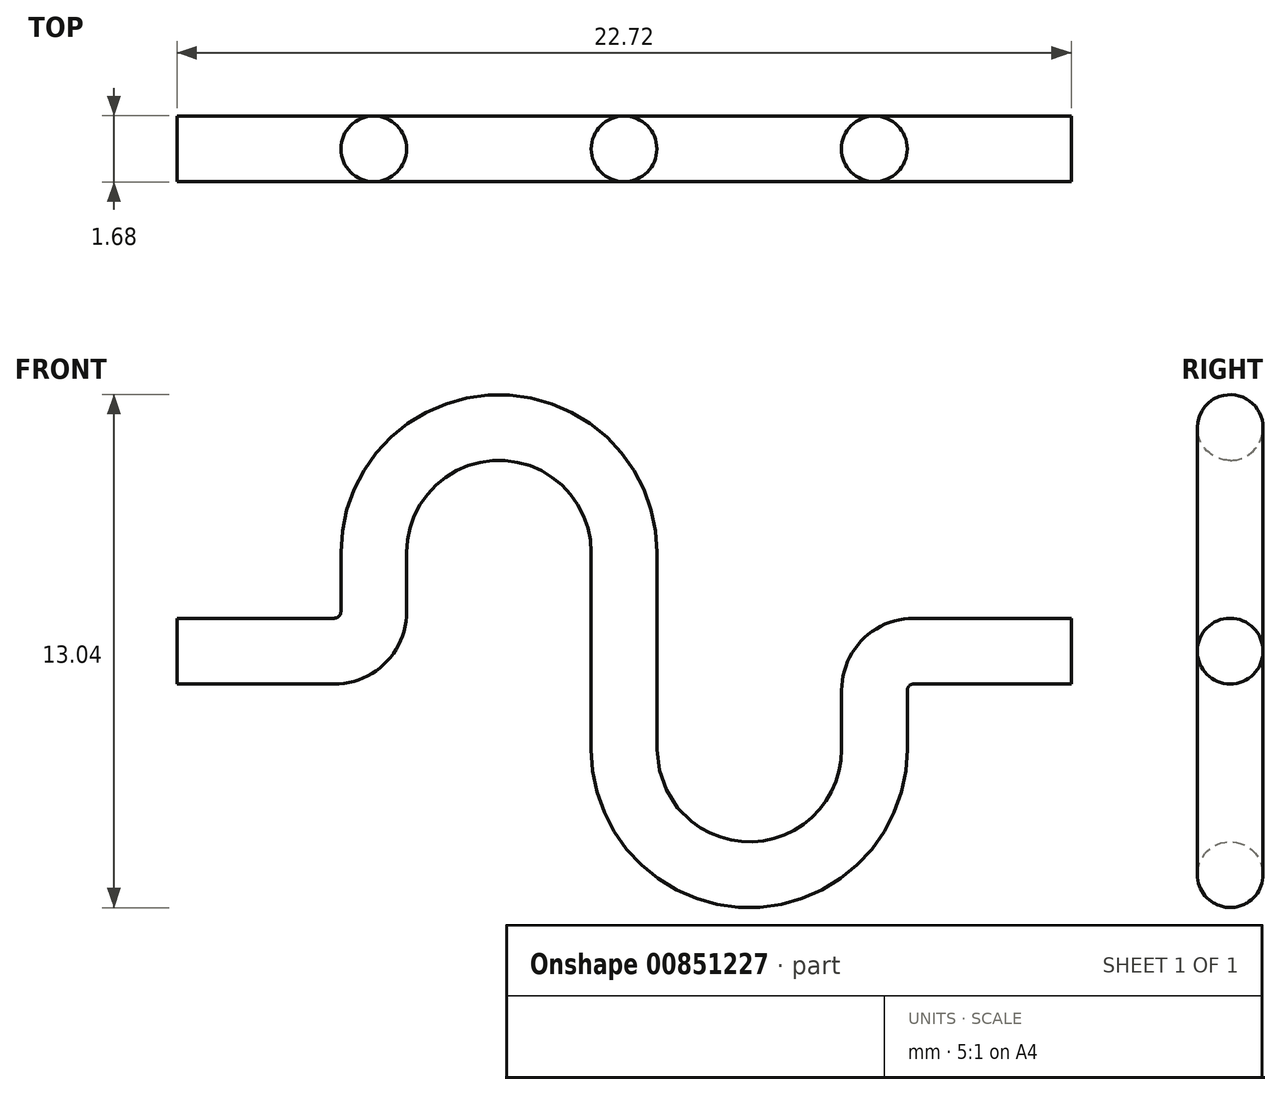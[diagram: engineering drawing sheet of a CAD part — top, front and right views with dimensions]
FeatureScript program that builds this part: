
annotation { "Feature Type Name" : "Feature", "Feature Type Description" : "" }
export const myFeature = defineFeature(function(context is Context, id is Id, definition is map)
    precondition{}
    {
        {
            var Q0;
            Q0=qCreatedBy(makeId("Front.planeOp"),FACE);
            var sketch = newSketch(context, id + "F0", { "sketchPlane" : qUnion([Q0])});
            skLineSegment(sketch, "E0", {"start": v(-9.36, 2.5) * mm, "end": v(9.36, 2.5) * mm, "construction": true});
            skLineSegment(sketch, "E1.MirrorCS", {"start": v(-9.36, -2.5) * mm, "end": v(9.36, -2.5) * mm, "construction": true});
            skArc(sketch, "E2", {"start": v(0, 2.5) * mm, "mid": v(-3.18, 5.68) * mm, "end": v(-6.36, 2.5) * mm});
            skLineSegment(sketch, "E3", {"start": v(0, 2.5) * mm, "end": v(0, -2.5) * mm});
            skArc(sketch, "E4", {"start": v(0, -2.5) * mm, "mid": v(3.18, -5.68) * mm, "end": v(6.36, -2.5) * mm});
            skLineSegment(sketch, "E5", {"start": v(-6.36, 2.5) * mm, "end": v(-6.36, 1) * mm});
            skLineSegment(sketch, "E6", {"start": v(6.36, -2.5) * mm, "end": v(6.36, -1) * mm});
            skLineSegment(sketch, "E7", {"start": v(-7.36, 0) * mm, "end": v(-11.36, 0) * mm});
            skLineSegment(sketch, "E8", {"start": v(7.36, 0) * mm, "end": v(11.36, 0) * mm});
            skPoint(sketch, "E9.visualSharp", {"position": v(-6.36, 0) * mm});
            skArc(sketch, "E9.filletArc", {"start": v(-7.36, 0) * mm, "mid": v(-6.65, 0.3) * mm, "end": v(-6.36, 1) * mm});
            skPoint(sketch, "E10.visualSharp", {"position": v(6.36, 0) * mm});
            skArc(sketch, "E10.filletArc", {"start": v(7.36, 0) * mm, "mid": v(6.65, -0.3) * mm, "end": v(6.36, -1) * mm});
            skSolve(sketch);
        }
        {
            var Q0;
            Q0=qCreatedBy(makeId("Right.planeOp"),FACE);
            var Q1;
            Q1=sQuery(id+"F0.wireOp",VERTEX,"E7.end");
            cPlane(context, id + "F1", {"entities" : qUnion([Q0, Q1]), "cplaneType" : CPlaneType.PLANE_POINT, "offset" : 25.4 * mm, "oppositeDirection" : true, "width" : 152.4 * mm, "height" : 152.4 * mm});
        }
        {
            var Q0;
            Q0=qCreatedBy(id+"F1.planeOp",FACE);
            var sketch = newSketch(context, id + "F2", { "sketchPlane" : qUnion([Q0])});
            skCircle(sketch, "E11", {"center": v(0, 0) * mm, "radius": 0.84 * mm});
            skSolve(sketch);
        }
        {
            var Q0;
            Q0=makeQuery(id+"F2.imprint","IMPRINT",FACE,{"disambiguationData":[TD([[makeQuery(id+"F2.imprint","IMPRINT",EDGE,{"derivedFrom":sQuery(id+"F2.wireOp",EDGE,"E11")}),1.0]])]});
            var Q1;
            Q1=sQuery(id+"F2.wireOp",EDGE,"E11");
            var Q2;
            Q2=sQuery(id+"F0.wireOp",EDGE,"E7");
            var Q3;
            Q3=sQuery(id+"F0.wireOp",EDGE,"E9.filletArc");
            var Q4;
            Q4=sQuery(id+"F0.wireOp",EDGE,"E5");
            var Q5;
            Q5=sQuery(id+"F0.wireOp",EDGE,"E2");
            var Q6;
            Q6=sQuery(id+"F0.wireOp",EDGE,"E3");
            var Q7;
            Q7=sQuery(id+"F0.wireOp",EDGE,"E4");
            var Q8;
            Q8=sQuery(id+"F0.wireOp",EDGE,"E6");
            var Q9;
            Q9=sQuery(id+"F0.wireOp",EDGE,"E10.filletArc");
            var Q10;
            Q10=sQuery(id+"F0.wireOp",EDGE,"E8");
            sweep(context, id + "F3", {"profiles" : qUnion([Q0]), "surfaceProfiles" : qUnion([Q1]), "path" : qUnion([Q2, Q3, Q4, Q5, Q6, Q7, Q8, Q9, Q10])});
        }
    });
